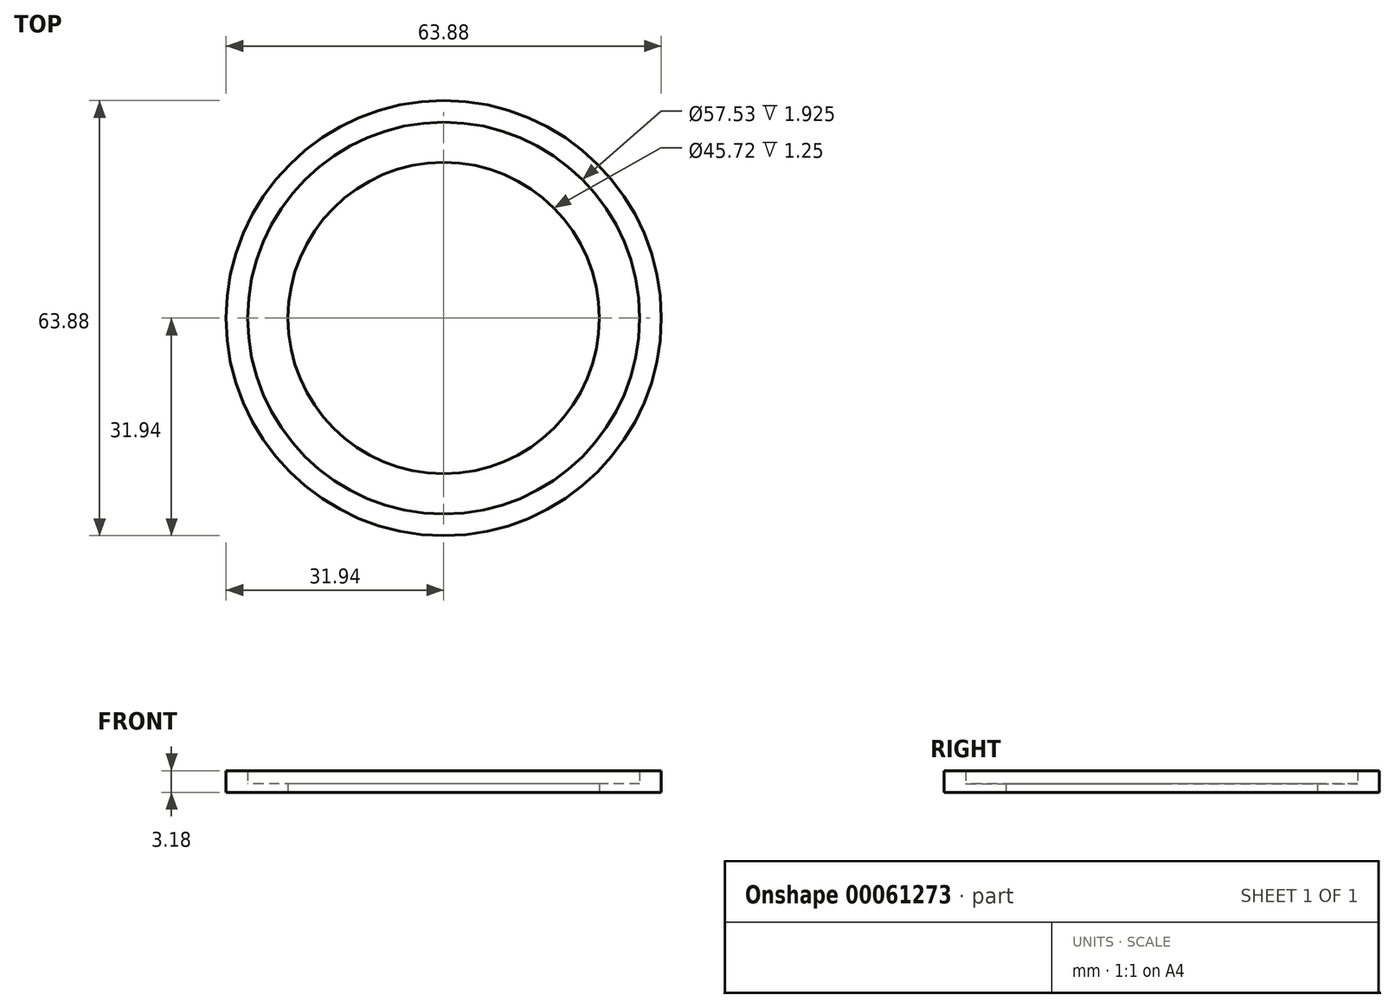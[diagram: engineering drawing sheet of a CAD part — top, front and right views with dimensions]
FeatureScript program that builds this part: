
annotation { "Feature Type Name" : "Feature", "Feature Type Description" : "" }
export const myFeature = defineFeature(function(context is Context, id is Id, definition is map)
    precondition{}
    {
        {
            assignVariable(context, id + "F0", {"name" : "Depth", "anyValue" : 1.25});
        }
        {
            var Q0;
            Q0=qCreatedBy(makeId("Top.planeOp"),FACE);
            var sketch = newSketch(context, id + "F1", { "sketchPlane" : qUnion([Q0])});
            skCircle(sketch, "E0", {"center": v(0, 0) * mm, "radius": 22.86 * mm});
            skCircle(sketch, "E1", {"center": v(0, 0) * mm, "radius": 28.77 * mm});
            skCircle(sketch, "E2", {"center": v(0, 0) * mm, "radius": 31.94 * mm});
            skSolve(sketch);
        }
        {
            var Q0;
            Q0=makeQuery(id+"F1.imprint","IMPRINT",FACE,{"disambiguationData":[TD([[makeQuery(id+"F1.imprint","IMPRINT",EDGE,{"derivedFrom":sQuery(id+"F1.wireOp",EDGE,"E1")}),-1.0]])]});
            extrude(context, id + "F2", {"entities" : qUnion([Q0]), "depth" : 3.17 * mm});
        }
        {
            var Q0;
            Q0=makeQuery(id+"F1.imprint","IMPRINT",FACE,{"disambiguationData":[TD([[makeQuery(id+"F1.imprint","IMPRINT",EDGE,{"derivedFrom":sQuery(id+"F1.wireOp",EDGE,"E0")}),-1.0]])]});
            extrude(context, id + "F3", {"entities" : qUnion([Q0]), "operationType" : NewBodyOperationType.ADD, "depth" : (getVariable(context, 'Depth')) * mm});
        }
    });
